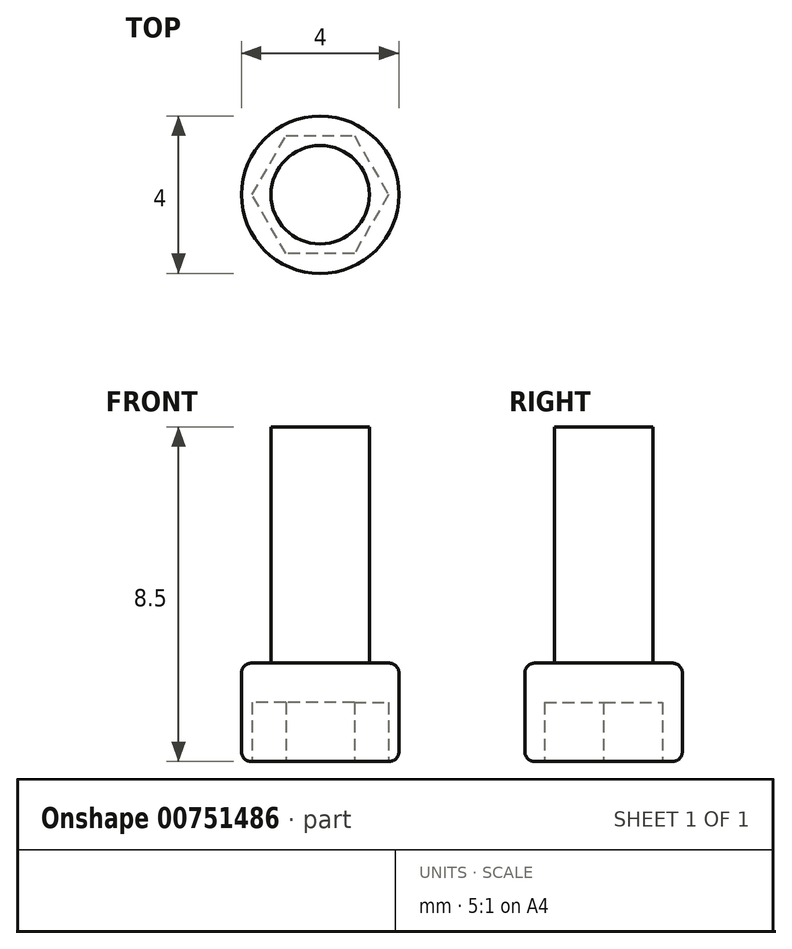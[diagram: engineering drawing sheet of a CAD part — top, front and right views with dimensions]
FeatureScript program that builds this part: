
annotation { "Feature Type Name" : "Feature", "Feature Type Description" : "" }
export const myFeature = defineFeature(function(context is Context, id is Id, definition is map)
    precondition{}
    {
        {
            var Q0;
            Q0=qCreatedBy(makeId("Top.planeOp"),FACE);
            var sketch = newSketch(context, id + "F0", { "sketchPlane" : qUnion([Q0])});
            skCircle(sketch, "E0", {"center": v(0, 0) * mm, "radius": 2 * mm});
            skCircle(sketch, "E1", {"center": v(0, 0) * mm, "radius": 1.25 * mm});
            skSolve(sketch);
        }
        {
            var Q0;
            Q0=makeQuery(id+"F0.imprint","IMPRINT",FACE,{"disambiguationData":[TD([[makeQuery(id+"F0.imprint","IMPRINT",EDGE,{"derivedFrom":sQuery(id+"F0.wireOp",EDGE,"E0")}),1.0]])]});
            extrude(context, id + "F1", {"entities" : qUnion([Q0]), "depth" : 2.5 * mm, "offsetDistance" : 25 * mm});
        }
        {
            var Q0;
            Q0=makeQuery(id+"F0.imprint","IMPRINT",FACE,{"disambiguationData":[TD([[makeQuery(id+"F0.imprint","IMPRINT",EDGE,{"derivedFrom":sQuery(id+"F0.wireOp",EDGE,"E1")}),1.0]])]});
            extrude(context, id + "F2", {"entities" : qUnion([Q0]), "operationType" : NewBodyOperationType.ADD, "depth" : 8.5 * mm, "offsetDistance" : 25 * mm});
        }
        {
            var Q0;
            Q0=makeQuery(id+"F0.imprint","IMPRINT",FACE,{"disambiguationData":[TD([[makeQuery(id+"F0.imprint","IMPRINT",EDGE,{"derivedFrom":sQuery(id+"F0.wireOp",EDGE,"E0")}),1.0]])]});
            var sketch = newSketch(context, id + "F3", { "sketchPlane" : qUnion([Q0])});
            skCircle(sketch, "E2.cCircle", {"center": v(0, 0) * mm, "radius": 1.5 * mm, "construction": true});
            skLineSegment(sketch, "E2.0", {"start": v(0.87, -1.5) * mm, "end": v(-0.87, -1.5) * mm});
            skLineSegment(sketch, "E2.1", {"start": v(-0.87, -1.5) * mm, "end": v(-1.73, 0) * mm});
            skLineSegment(sketch, "E2.2", {"start": v(-1.73, 0) * mm, "end": v(-0.87, 1.5) * mm});
            skLineSegment(sketch, "E2.3", {"start": v(-0.87, 1.5) * mm, "end": v(0.87, 1.5) * mm});
            skLineSegment(sketch, "E2.4", {"start": v(0.87, 1.5) * mm, "end": v(1.73, 0) * mm});
            skLineSegment(sketch, "E2.5", {"start": v(1.73, 0) * mm, "end": v(0.87, -1.5) * mm});
            skPoint(sketch, "E2.0.midPoint", {"position": v(0, -1.5) * mm});
            skSolve(sketch);
        }
        {
            var Q0;
            Q0=makeQuery(id+"F0.imprint","IMPRINT",FACE,{"disambiguationData":[TD([[makeQuery(id+"F0.imprint","IMPRINT",EDGE,{"derivedFrom":sQuery(id+"F0.wireOp",EDGE,"E1")}),1.0]])]});
            var Q1;
            Q1=makeQuery(id+"F3.imprint","IMPRINT",FACE,{"disambiguationData":[TD([[makeQuery(id+"F3.imprint","IMPRINT",EDGE,{"derivedFrom":sQuery(id+"F3.wireOp",EDGE,"E2.0")}),-1.0]])]});
            var Q2;
            Q2=makeQuery(id+"F3.imprint","IMPRINT",FACE,{"disambiguationData":[TD([[makeQuery(id+"F3.imprint","IMPRINT",EDGE,{"derivedFrom":makeQuery(id+"F0.imprint","IMPRINT",EDGE,{"derivedFrom":sQuery(id+"F0.wireOp",EDGE,"E1")})}),1.0]])]});
            var Q3;
            Q3=makeQuery(id+"F2.opExtrude","CAP_FACE",FACE,{"disambiguationData":[OSD([sQuery(id+"F0.wireOp",EDGE,"E1")])],"isStart":false});
            extrude(context, id + "F4", {"entities" : qUnion([Q0, Q1, Q2, Q3]), "operationType" : NewBodyOperationType.REMOVE, "depth" : 1.5 * mm, "offsetDistance" : 25 * mm});
        }
        {
            var Q0;
            Q0=makeQuery(id+"F1.opExtrude","CAP_EDGE",EDGE,{"disambiguationData":[OSD([sQuery(id+"F0.wireOp",EDGE,"E1")])],"isStart":false});
            var Q1;
            Q1=makeQuery(id+"F1.opExtrude","CAP_EDGE",EDGE,{"disambiguationData":[OSD([sQuery(id+"F0.wireOp",EDGE,"E0")])],"isStart":false});
            var Q2;
            Q2=makeQuery(id+"F1.opExtrude","CAP_EDGE",EDGE,{"disambiguationData":[OSD([sQuery(id+"F0.wireOp",EDGE,"E0")])],"isStart":true});
            fillet(context, id + "F5", {"entities" : qUnion([Q0, Q1, Q2]), "radius" : .25 * mm, "tangentPropagation" : true, "allowEdgeOverflow" : false});
        }
    });
